# Revit family: Parex_AirTerminal_Amore900
name_source: partatom
category: Air Terminals
units: mm (PartAtom-declared; Revit-internal decimal feet)

## family parameters
Cut with Voids When Loaded = No
Host = Face
Part Type = Normal
Room Calculation Point = No
Round Connector Dimension = Use Diameter
Shared = No

## types (1)
- Parex_AirTerminal_Amore900
    BaseHeight = 35 mm  [stored 0.114829 ft]
    BasePlateThickness = 60 mm
    Calc_DektiteMidDiameter = 180 mm  [stored 0.590551 ft]
    ChimneyDiameter = 160 mm  [stored 0.524934 ft]
    ChimneyLength = 100 mm  [stored 0.328084 ft]
    Default Elevation = 1219 mm
    Dektite_Diameter = 200 mm  [stored 0.656168 ft]
    Description = Amore 900 Normal Cooking
    Export Type to IFC As = IfcAirTerminalType
    GrillMaterial = Parex_ASA Plastic_Green_Cutout
    Height = 198 mm  [stored 0.649606 ft]
    Manufacturer = Amore Homes
    Material = Parex_ASA Plastic_Green
    Model = AM900
    Specifications = 900 m3/hr airflow

Energy efficient German made EX-Motor

The motor housing is crafted from ASA, one of the most durable plastics for direct sunlight exposure

200mm flexi ducting (5m), solid roof extension pipe and bell housing adapter included with motor.

Installation: Roof & Wall
    Type IFC Predefined Type = DIFFUSER
    URL = https://amorehomes.co.nz
    WarrantyDescription = 10 years
    Width = 278 mm  [stored 0.912073 ft]

note: [stored X ft] marks values corroborated as IEEE doubles in the binary element streams (Revit-internal decimal feet)

## geometry (parser evidence)
native form markers: Extrusion x1, Sweep x4
no freeform markers — native parametric forms only
